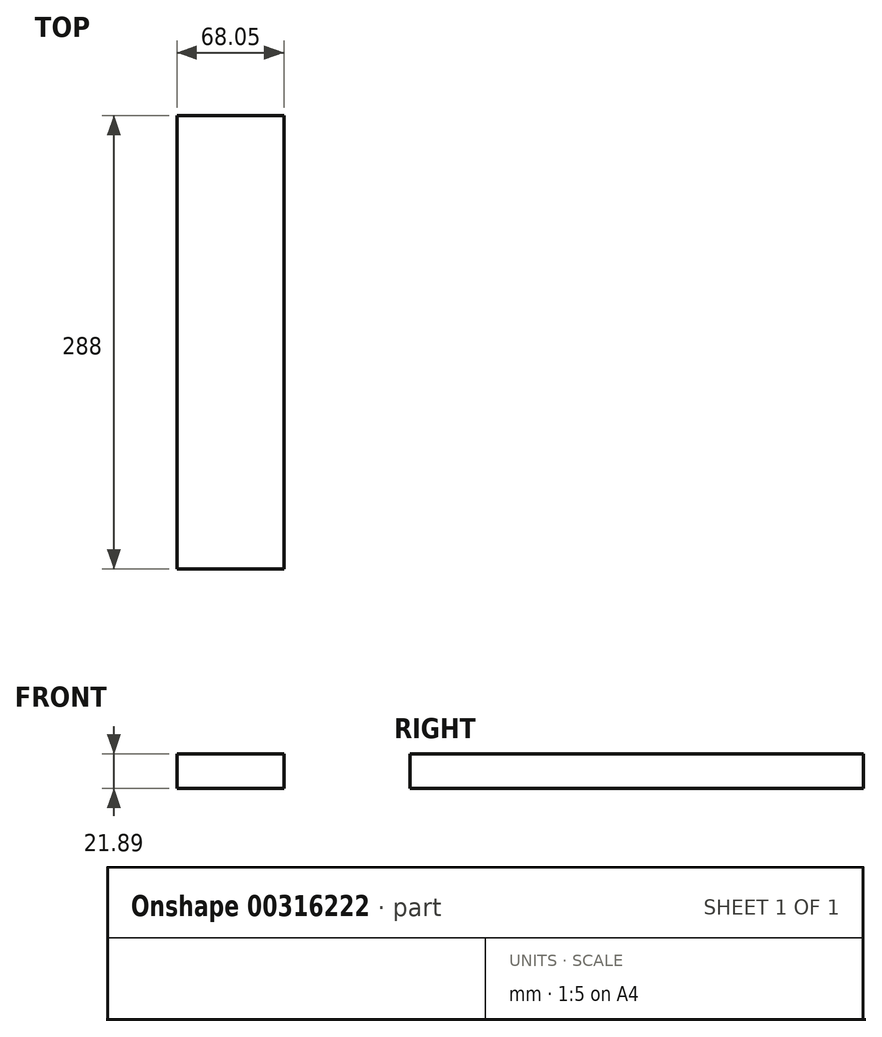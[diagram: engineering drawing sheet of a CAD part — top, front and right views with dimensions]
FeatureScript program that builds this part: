
annotation { "Feature Type Name" : "Feature", "Feature Type Description" : "" }
export const myFeature = defineFeature(function(context is Context, id is Id, definition is map)
    precondition{}
    {
        {
            var Q0;
            Q0=qCreatedBy(makeId("Front.planeOp"),FACE);
            var sketch = newSketch(context, id + "F0", { "sketchPlane" : qUnion([Q0])});
            skLineSegment(sketch, "E0.bottom", {"start": v(-2333.92, -674.82) * mm, "end": v(-2265.87, -674.82) * mm});
            skLineSegment(sketch, "E0.top", {"start": v(-2333.92, -652.93) * mm, "end": v(-2265.87, -652.93) * mm});
            skLineSegment(sketch, "E0.left", {"start": v(-2333.92, -652.93) * mm, "end": v(-2333.92, -674.82) * mm});
            skLineSegment(sketch, "E0.right", {"start": v(-2265.87, -652.93) * mm, "end": v(-2265.87, -674.82) * mm});
            skSolve(sketch);
        }
        {
            var Q0;
            Q0 = qSketchRegion(id + "F0", true);
            extrude(context, id + "F1", {"entities" : qUnion([Q0]), "depth" : 288 * mm});
        }
    });
